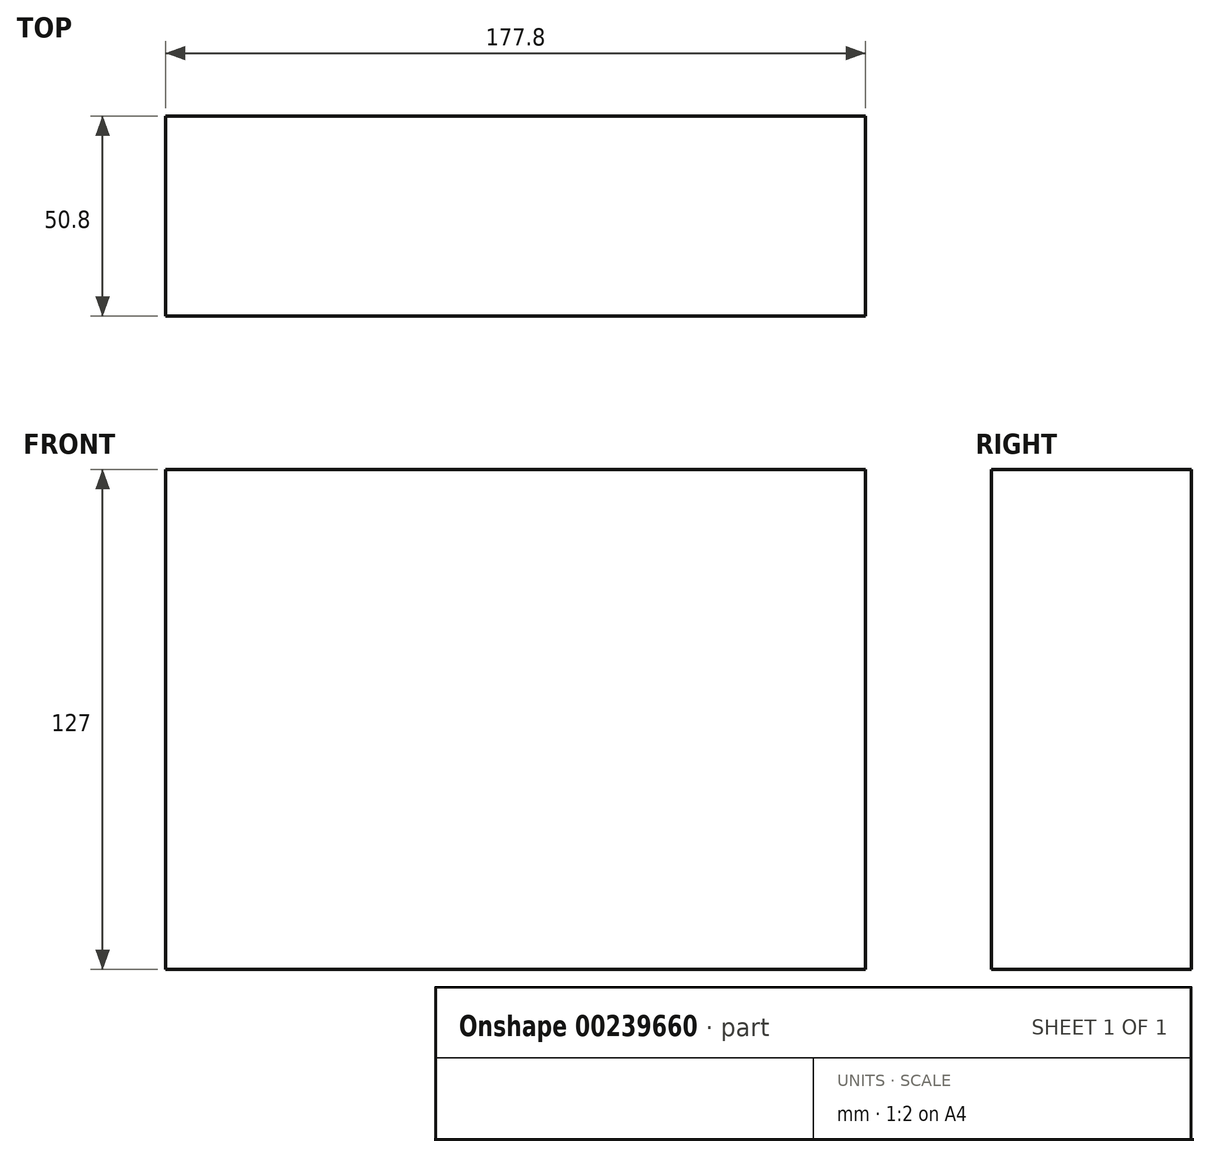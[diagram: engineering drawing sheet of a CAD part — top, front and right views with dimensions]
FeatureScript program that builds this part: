
annotation { "Feature Type Name" : "Feature", "Feature Type Description" : "" }
export const myFeature = defineFeature(function(context is Context, id is Id, definition is map)
    precondition{}
    {
        {
            var Q0;
            Q0=qCreatedBy(makeId("Front.planeOp"),FACE);
            var sketch = newSketch(context, id + "F0", { "sketchPlane" : qUnion([Q0])});
            skLineSegment(sketch, "E0.bottom", {"start": v(-69.23, 48.47) * mm, "end": v(108.57, 48.47) * mm});
            skLineSegment(sketch, "E0.top", {"start": v(-69.23, -78.53) * mm, "end": v(108.57, -78.53) * mm});
            skLineSegment(sketch, "E0.left", {"start": v(-69.23, 48.47) * mm, "end": v(-69.23, -78.53) * mm});
            skLineSegment(sketch, "E0.right", {"start": v(108.57, 48.47) * mm, "end": v(108.57, -78.53) * mm});
            skSolve(sketch);
        }
        {
            var Q0;
            Q0=makeQuery(id+"F0.imprint","IMPRINT",FACE,{"disambiguationData":[TD([[makeQuery(id+"F0.imprint","IMPRINT",EDGE,{"derivedFrom":sQuery(id+"F0.wireOp",EDGE,"E0.bottom")}),-1.0]])]});
            extrude(context, id + "F1", {"entities" : qUnion([Q0]), "depth" : 50.8 * mm});
        }
    });
